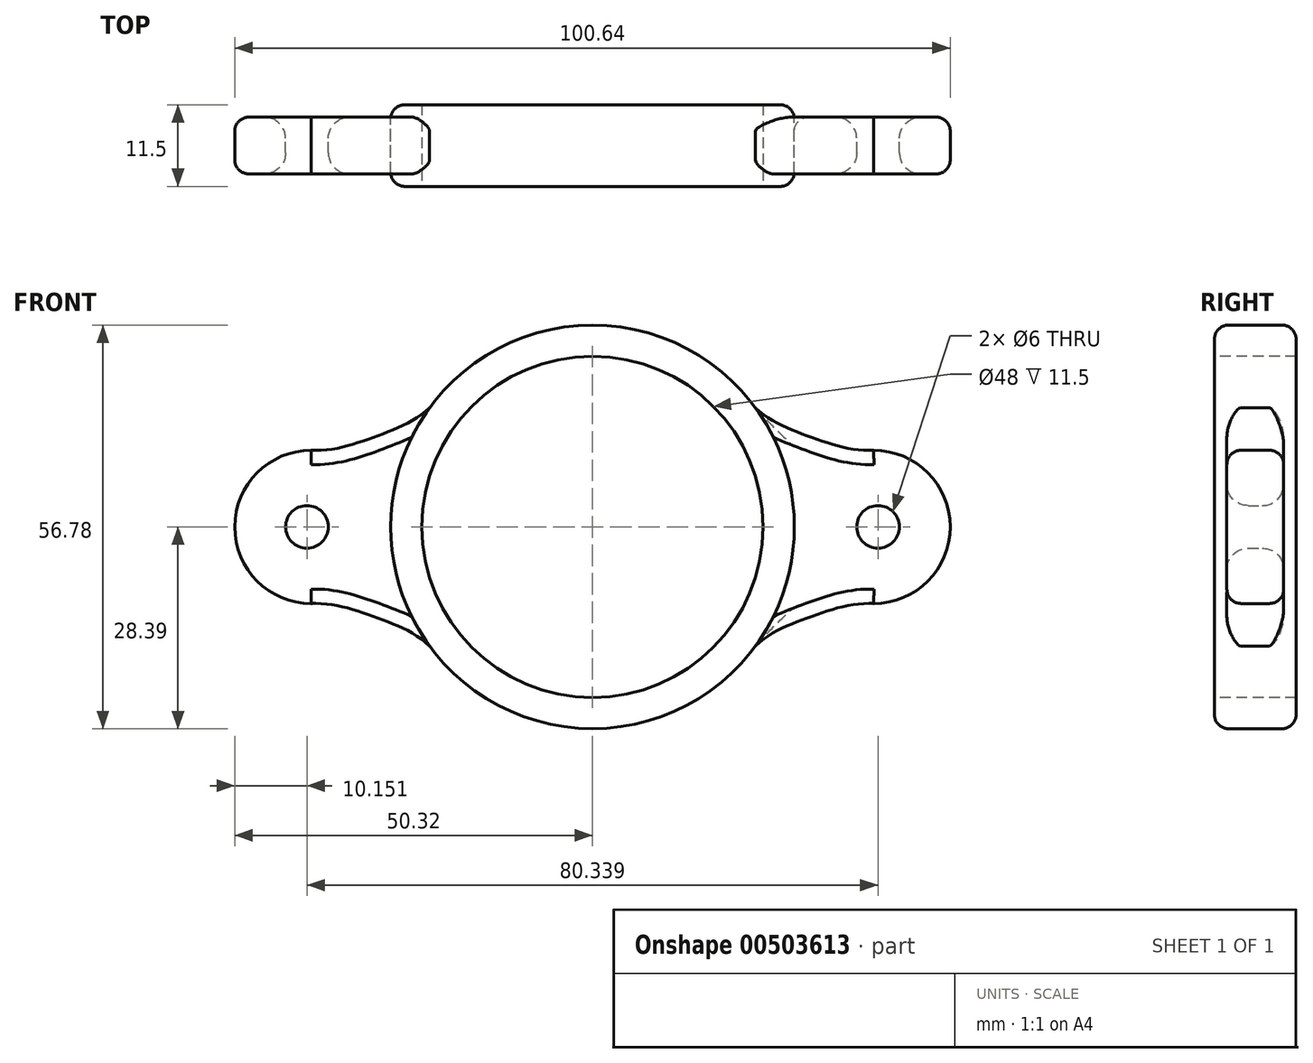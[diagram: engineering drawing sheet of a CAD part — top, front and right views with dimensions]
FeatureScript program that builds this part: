
annotation { "Feature Type Name" : "Feature", "Feature Type Description" : "" }
export const myFeature = defineFeature(function(context is Context, id is Id, definition is map)
    precondition{}
    {
        {
            assignVariable(context, id + "F0", {"name" : "wingDepth", "anyValue" : 8});
        }
        {
            assignVariable(context, id + "F1", {"name" : "bodyDepth", "anyValue" : 11.5});
        }
        {
            var Q0;
            Q0=qCreatedBy(makeId("Front.planeOp"),FACE);
            var sketch = newSketch(context, id + "F2", { "sketchPlane" : qUnion([Q0])});
            skCircle(sketch, "E0", {"center": v(0, 0) * mm, "radius": 28.39 * mm});
            skCircle(sketch, "E1", {"center": v(39.55, 0) * mm, "radius": 10.78 * mm});
            skFitSpline(sketch, "E2", {"points": [v(39.55, 10.78) * mm, v(30.04, 12.9) * mm, v(22.92, 16.74) * mm], "startDerivative": vector(-19.27, -1.04) * mm, "endDerivative": vector(-14, 12.97) * mm});
            skFitSpline(sketch, "E3.MirrorCS", {"points": [v(39.55, -10.78) * mm, v(30.04, -12.9) * mm, v(22.92, -16.74) * mm], "startDerivative": vector(-19.27, 1.04) * mm, "endDerivative": vector(-14, -12.97) * mm});
            skFitSpline(sketch, "E4.MirrorCS", {"points": [v(-39.55, 10.78) * mm, v(-30.04, 12.9) * mm, v(-22.92, 16.74) * mm], "startDerivative": vector(19.27, -1.04) * mm, "endDerivative": vector(14, 12.97) * mm});
            skCircle(sketch, "E5.MirrorC", {"center": v(-39.55, 0) * mm, "radius": 10.78 * mm});
            skFitSpline(sketch, "E6.MirrorCS", {"points": [v(-39.55, -10.78) * mm, v(-30.04, -12.9) * mm, v(-22.92, -16.74) * mm], "startDerivative": vector(19.27, 1.04) * mm, "endDerivative": vector(14, -12.97) * mm});
            skSolve(sketch);
        }
        {
            var Q0;
            {var subQ0=sQuery(id+"F2.wireOp",EDGE,"E5.MirrorC");var subQ1=sQuery(id+"F2.wireOp",EDGE,"E4.MirrorCS");var subQ2=makeQuery(id+"F2.imprint","INTERSECT",VERTEX,{"disambiguationData":[OD(0.0)],"derivedFrom":[subQ1,subQ0]});Q0=makeQuery(id+"F2.imprint","IMPRINT",FACE,{"disambiguationData":[TD([[makeQuery(id+"F2.imprint","IMPRINT",EDGE,{"disambiguationData":[TD([[subQ2,-1.0]])],"derivedFrom":subQ1}),-1.0]])]});}
            var Q1;
            {var subQ0=sQuery(id+"F2.wireOp",EDGE,"E4.MirrorCS");var subQ1=sQuery(id+"F2.wireOp",EDGE,"E0");var subQ2=makeQuery(id+"F2.imprint","INTERSECT",VERTEX,{"derivedFrom":[subQ1,subQ0]});Q1=makeQuery(id+"F2.imprint","IMPRINT",FACE,{"disambiguationData":[TD([[makeQuery(id+"F2.imprint","IMPRINT",EDGE,{"disambiguationData":[TD([[subQ2,-1.0]])],"derivedFrom":subQ1}),-1.0]])]});}
            var Q2;
            {var subQ0=sQuery(id+"F2.wireOp",EDGE,"E2");var subQ1=sQuery(id+"F2.wireOp",EDGE,"E0");var subQ2=makeQuery(id+"F2.imprint","INTERSECT",VERTEX,{"derivedFrom":[subQ1,subQ0]});Q2=makeQuery(id+"F2.imprint","IMPRINT",FACE,{"disambiguationData":[TD([[makeQuery(id+"F2.imprint","IMPRINT",EDGE,{"disambiguationData":[TD([[subQ2,1.0]])],"derivedFrom":subQ1}),-1.0]])]});}
            var Q3;
            {var subQ0=sQuery(id+"F2.wireOp",EDGE,"E2");var subQ1=sQuery(id+"F2.wireOp",EDGE,"E1");var subQ2=makeQuery(id+"F2.imprint","INTERSECT",VERTEX,{"disambiguationData":[OD(1.0)],"derivedFrom":[subQ1,subQ0]});Q3=makeQuery(id+"F2.imprint","IMPRINT",FACE,{"disambiguationData":[TD([[makeQuery(id+"F2.imprint","IMPRINT",EDGE,{"disambiguationData":[TD([[subQ2,-1.0]])],"derivedFrom":subQ1}),1.0]])]});}
            extrude(context, id + "F3", {"entities" : qUnion([Q0, Q1, Q2, Q3]), "depth" : (getVariable(context, 'wingDepth')) * mm, "symmetric" : true});
        }
        {
            var Q0;
            Q0=qCreatedBy(makeId("Front.planeOp"),FACE);
            var sketch = newSketch(context, id + "F4", { "sketchPlane" : qUnion([Q0])});
            skCircle(sketch, "E7", {"center": v(0, 0) * mm, "radius": 8 * mm});
            skCircle(sketch, "E8", {"center": v(0, 0) * mm, "radius": 24 * mm});
            skSolve(sketch);
        }
        {
            var Q0;
            {var subQ0=sQuery(id+"F2.wireOp",EDGE,"E0");var subQ1=makeQuery(id+"F2.imprint","INTERSECT",VERTEX,{"derivedFrom":[subQ0,sQuery(id+"F2.wireOp",EDGE,"E2")]});Q0=makeQuery(id+"F2.imprint","IMPRINT",FACE,{"disambiguationData":[TD([[makeQuery(id+"F2.imprint","IMPRINT",EDGE,{"disambiguationData":[TD([[subQ1,-1.0]])],"derivedFrom":subQ0}),1.0]])]});}
            extrude(context, id + "F5", {"entities" : qUnion([Q0]), "depth" : (getVariable(context, 'bodyDepth')) * mm, "symmetric" : true});
        }
        {
            var Q0;
            Q0 = qSketchRegion(id + "F4", true);
            extrude(context, id + "F6", {"entities" : qUnion([Q0]), "operationType" : NewBodyOperationType.REMOVE, "oppositeDirection" : true, "depth" : (2 * getVariable(context, 'bodyDepth')) * mm, "symmetric" : true});
        }
        {
            var Q0;
            Q0=qCreatedBy(makeId("Front.planeOp"),FACE);
            var sketch = newSketch(context, id + "F7", { "sketchPlane" : qUnion([Q0])});
            skCircle(sketch, "E9", {"center": v(0, 0) * mm, "radius": 11.3 * mm});
            skSolve(sketch);
        }
        {
            var Q0;
            Q0 = qSketchRegion(id + "F7", true);
            extrude(context, id + "F8", {"entities" : qUnion([Q0]), "operationType" : NewBodyOperationType.REMOVE, "oppositeDirection" : true, "depth" : (2 * getVariable(context, 'bodyDepth')) * mm, "symmetric" : true});
        }
        {
            var Q0;
            Q0=makeQuery(id+"F3.opExtrude","CAP_EDGE",EDGE,{"disambiguationData":[OSD([sQuery(id+"F2.wireOp",EDGE,"E5.MirrorC")])],"isStart":true});
            var Q1;
            Q1=makeQuery(id+"F3.opExtrude","CAP_EDGE",EDGE,{"disambiguationData":[OSD([sQuery(id+"F2.wireOp",EDGE,"E4.MirrorCS")])],"isStart":true});
            var Q2;
            Q2=makeQuery(id+"F3.opExtrude","CAP_EDGE",EDGE,{"disambiguationData":[OSD([sQuery(id+"F2.wireOp",EDGE,"E4.MirrorCS")])],"isStart":false});
            var Q3;
            Q3=makeQuery(id+"F3.opExtrude","CAP_EDGE",EDGE,{"disambiguationData":[OSD([sQuery(id+"F2.wireOp",EDGE,"E5.MirrorC")])],"isStart":false});
            var Q4;
            Q4=makeQuery(id+"F3.opExtrude","CAP_EDGE",EDGE,{"disambiguationData":[OSD([sQuery(id+"F2.wireOp",EDGE,"E6.MirrorCS")])],"isStart":false});
            var Q5;
            Q5=makeQuery(id+"F3.opExtrude","CAP_EDGE",EDGE,{"disambiguationData":[OSD([sQuery(id+"F2.wireOp",EDGE,"E6.MirrorCS")])],"isStart":true});
            var Q6;
            Q6=makeQuery(id+"F3.opExtrude","CAP_EDGE",EDGE,{"disambiguationData":[OSD([sQuery(id+"F2.wireOp",EDGE,"E1")])],"isStart":false});
            var Q7;
            Q7=makeQuery(id+"F3.opExtrude","CAP_EDGE",EDGE,{"disambiguationData":[OSD([sQuery(id+"F2.wireOp",EDGE,"E2")])],"isStart":false});
            var Q8;
            Q8=makeQuery(id+"F3.opExtrude","CAP_EDGE",EDGE,{"disambiguationData":[OSD([sQuery(id+"F2.wireOp",EDGE,"E3.MirrorCS")])],"isStart":false});
            var Q9;
            Q9=makeQuery(id+"F5.opExtrude","CAP_EDGE",EDGE,{"disambiguationData":[OSD([sQuery(id+"F2.wireOp",EDGE,"E0")])],"isStart":false});
            var Q10;
            Q10=makeQuery(id+"F3.opExtrude","CAP_EDGE",EDGE,{"disambiguationData":[OSD([sQuery(id+"F2.wireOp",EDGE,"E2")])],"isStart":true});
            var Q11;
            Q11=makeQuery(id+"F3.opExtrude","CAP_FACE",FACE,{"disambiguationData":[OSD([sQuery(id+"F2.wireOp",EDGE,"E0"),sQuery(id+"F2.wireOp",EDGE,"E1"),sQuery(id+"F2.wireOp",EDGE,"E2"),sQuery(id+"F2.wireOp",EDGE,"E3.MirrorCS")])],"isStart":true});
            var Q12;
            Q12=makeQuery(id+"F5.opExtrude","CAP_EDGE",EDGE,{"disambiguationData":[OSD([sQuery(id+"F2.wireOp",EDGE,"E0")])],"isStart":true});
            fillet(context, id + "F9", {"entities" : qUnion([Q0, Q1, Q2, Q3, Q4, Q5, Q6, Q7, Q8, Q9, Q10, Q11, Q12]), "radius" : 2 * mm, "tangentPropagation" : true, "allowEdgeOverflow" : false});
        }
        {
            var Q0;
            Q0=qCreatedBy(makeId("Front.planeOp"),FACE);
            var sketch = newSketch(context, id + "F10", { "sketchPlane" : qUnion([Q0])});
            skCircle(sketch, "E10", {"center": v(-40.17, 0) * mm, "radius": 3 * mm});
            skCircle(sketch, "E11.MirrorC", {"center": v(40.17, 0) * mm, "radius": 3 * mm});
            skSolve(sketch);
        }
        {
            var Q0;
            Q0 = qSketchRegion(id + "F10", true);
            extrude(context, id + "F11", {"entities" : qUnion([Q0]), "operationType" : NewBodyOperationType.REMOVE, "depth" : (2 * getVariable(context, 'wingDepth')) * mm, "symmetric" : true});
        }
        {
            var Q0;
            Q0=makeQuery(id+"F11.boolean.opBoolean","INTERSECT",EDGE,{"derivedFrom":[makeQuery(id+"F3.opExtrude","CAP_FACE",FACE,{"disambiguationData":[OSD([sQuery(id+"F2.wireOp",EDGE,"E0"),sQuery(id+"F2.wireOp",EDGE,"E1"),sQuery(id+"F2.wireOp",EDGE,"E2"),sQuery(id+"F2.wireOp",EDGE,"E3.MirrorCS")])],"isStart":true}),makeQuery(id+"F11.opExtrude","SWEPT_FACE",FACE,{"disambiguationData":[OSD([sQuery(id+"F10.wireOp",EDGE,"E11.MirrorC")])]})]});
            var Q1;
            Q1=makeQuery(id+"F11.boolean.opBoolean","INTERSECT",EDGE,{"derivedFrom":[makeQuery(id+"F3.opExtrude","CAP_FACE",FACE,{"disambiguationData":[OSD([sQuery(id+"F2.wireOp",EDGE,"E0"),sQuery(id+"F2.wireOp",EDGE,"E4.MirrorCS"),sQuery(id+"F2.wireOp",EDGE,"E5.MirrorC"),sQuery(id+"F2.wireOp",EDGE,"E6.MirrorCS")])],"isStart":true}),makeQuery(id+"F11.opExtrude","SWEPT_FACE",FACE,{"disambiguationData":[OSD([sQuery(id+"F10.wireOp",EDGE,"E10")])]})]});
            var Q2;
            Q2=makeQuery(id+"F11.boolean.opBoolean","INTERSECT",EDGE,{"derivedFrom":[makeQuery(id+"F3.opExtrude","CAP_FACE",FACE,{"disambiguationData":[OSD([sQuery(id+"F2.wireOp",EDGE,"E0"),sQuery(id+"F2.wireOp",EDGE,"E4.MirrorCS"),sQuery(id+"F2.wireOp",EDGE,"E5.MirrorC"),sQuery(id+"F2.wireOp",EDGE,"E6.MirrorCS")])],"isStart":false}),makeQuery(id+"F11.opExtrude","SWEPT_FACE",FACE,{"disambiguationData":[OSD([sQuery(id+"F10.wireOp",EDGE,"E10")])]})]});
            var Q3;
            Q3=makeQuery(id+"F11.boolean.opBoolean","INTERSECT",EDGE,{"derivedFrom":[makeQuery(id+"F3.opExtrude","CAP_FACE",FACE,{"disambiguationData":[OSD([sQuery(id+"F2.wireOp",EDGE,"E0"),sQuery(id+"F2.wireOp",EDGE,"E1"),sQuery(id+"F2.wireOp",EDGE,"E2"),sQuery(id+"F2.wireOp",EDGE,"E3.MirrorCS")])],"isStart":false}),makeQuery(id+"F11.opExtrude","SWEPT_FACE",FACE,{"disambiguationData":[OSD([sQuery(id+"F10.wireOp",EDGE,"E11.MirrorC")])]})]});
            fillet(context, id + "F12", {"entities" : qUnion([Q0, Q1, Q2, Q3]), "radius" : 3 * mm, "tangentPropagation" : true, "allowEdgeOverflow" : false});
        }
    });
